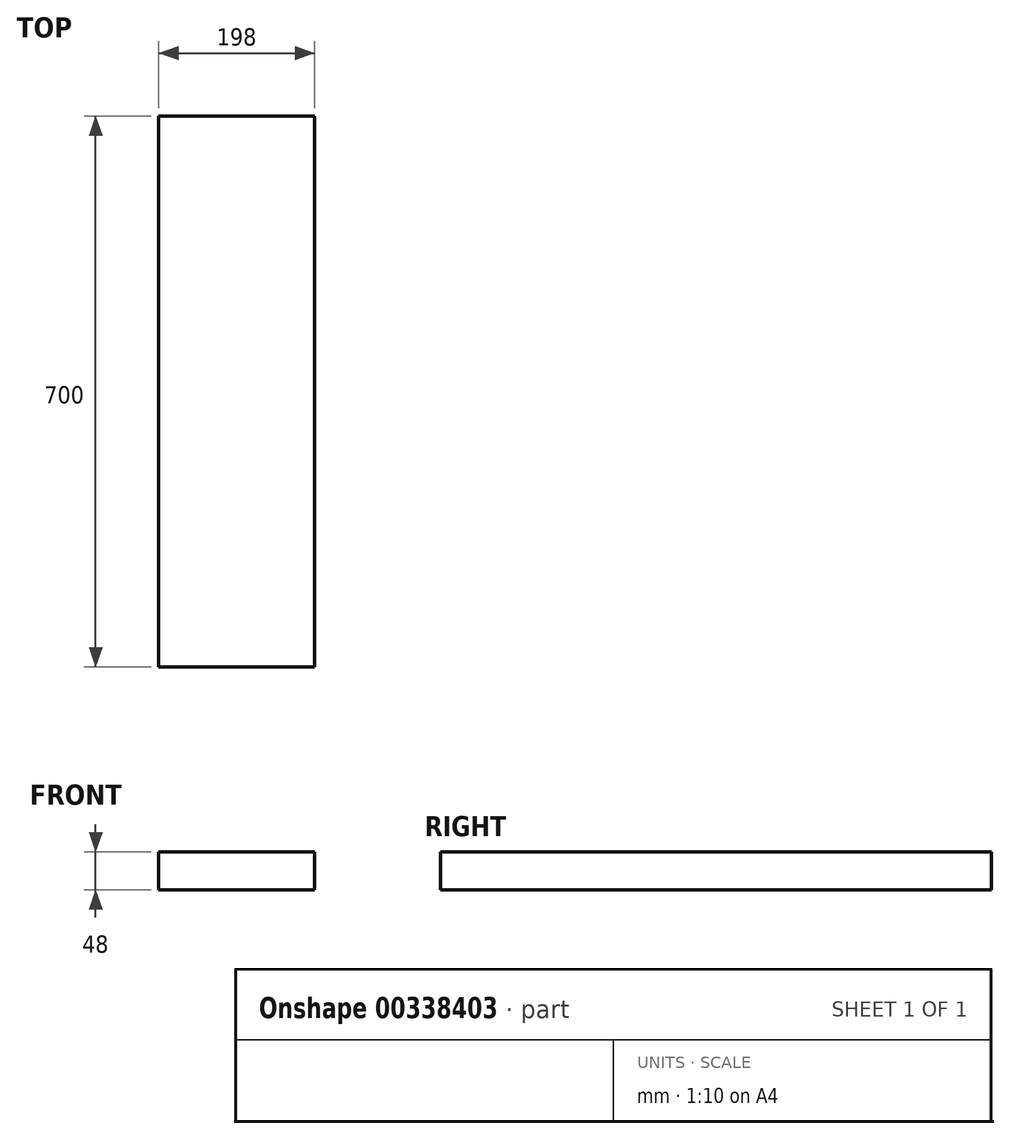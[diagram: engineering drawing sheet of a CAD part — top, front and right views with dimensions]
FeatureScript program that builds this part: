
annotation { "Feature Type Name" : "Feature", "Feature Type Description" : "" }
export const myFeature = defineFeature(function(context is Context, id is Id, definition is map)
    precondition{}
    {
        {
            var Q0;
            Q0=qCreatedBy(makeId("Front.planeOp"),FACE);
            var sketch = newSketch(context, id + "F0", { "sketchPlane" : qUnion([Q0])});
            skLineSegment(sketch, "E0.bottom", {"start": v(-99, -24) * mm, "end": v(99, -24) * mm});
            skLineSegment(sketch, "E0.top", {"start": v(-99, 24) * mm, "end": v(99, 24) * mm});
            skLineSegment(sketch, "E0.left", {"start": v(-99, -24) * mm, "end": v(-99, 24) * mm});
            skLineSegment(sketch, "E0.right", {"start": v(99, -24) * mm, "end": v(99, 24) * mm});
            skPoint(sketch, "E0.middle", {"position": v(0, 0) * mm});
            skSolve(sketch);
        }
        {
            var Q0;
            Q0=makeQuery(id+"F0.imprint","IMPRINT",FACE,{"disambiguationData":[TD([[makeQuery(id+"F0.imprint","IMPRINT",EDGE,{"derivedFrom":sQuery(id+"F0.wireOp",EDGE,"E0.bottom")}),1.0]])]});
            extrude(context, id + "F1", {"entities" : qUnion([Q0]), "offsetDistance" : 25 * mm, "depth" : 700 * mm});
        }
    });
